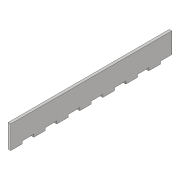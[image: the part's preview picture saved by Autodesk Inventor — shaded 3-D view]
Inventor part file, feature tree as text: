
AUTODESK INVENTOR PART (.ipt)
format: ipt  version: 2017 (Build 210142000, 142)  size: 114,176 bytes
history: native  units: in
note: dims shown in document units (in); Inventor stores cm internally (conversion verified against a paired STEP export)
features: extrude x2, sketch x2
ambient origin geometry x8: Origin, YZ Plane, XZ Plane, XY Plane, X Axis, Y Axis, Z Axis, Center Point
bodies: Solid1 (feature_tree)
feature tree (4):
  extrude  "Extrusion1"  Depth=1.0in
  extrude  "Extrusion2"  Depth=0.115in TaperAngle=0.0deg
  sketch  "Sketch1"  dims[d0=7.0in d1=1.0in]
  sketch  "Sketch2"  dims[d2=0.0in d3=0.115in d4=0.0in d5=0.5in d6=0.115in d7=0.5in d8=2.7559in d10=1.0in d11=0.3937in d13=1.0in d15=0.115in d16=0.0in]
